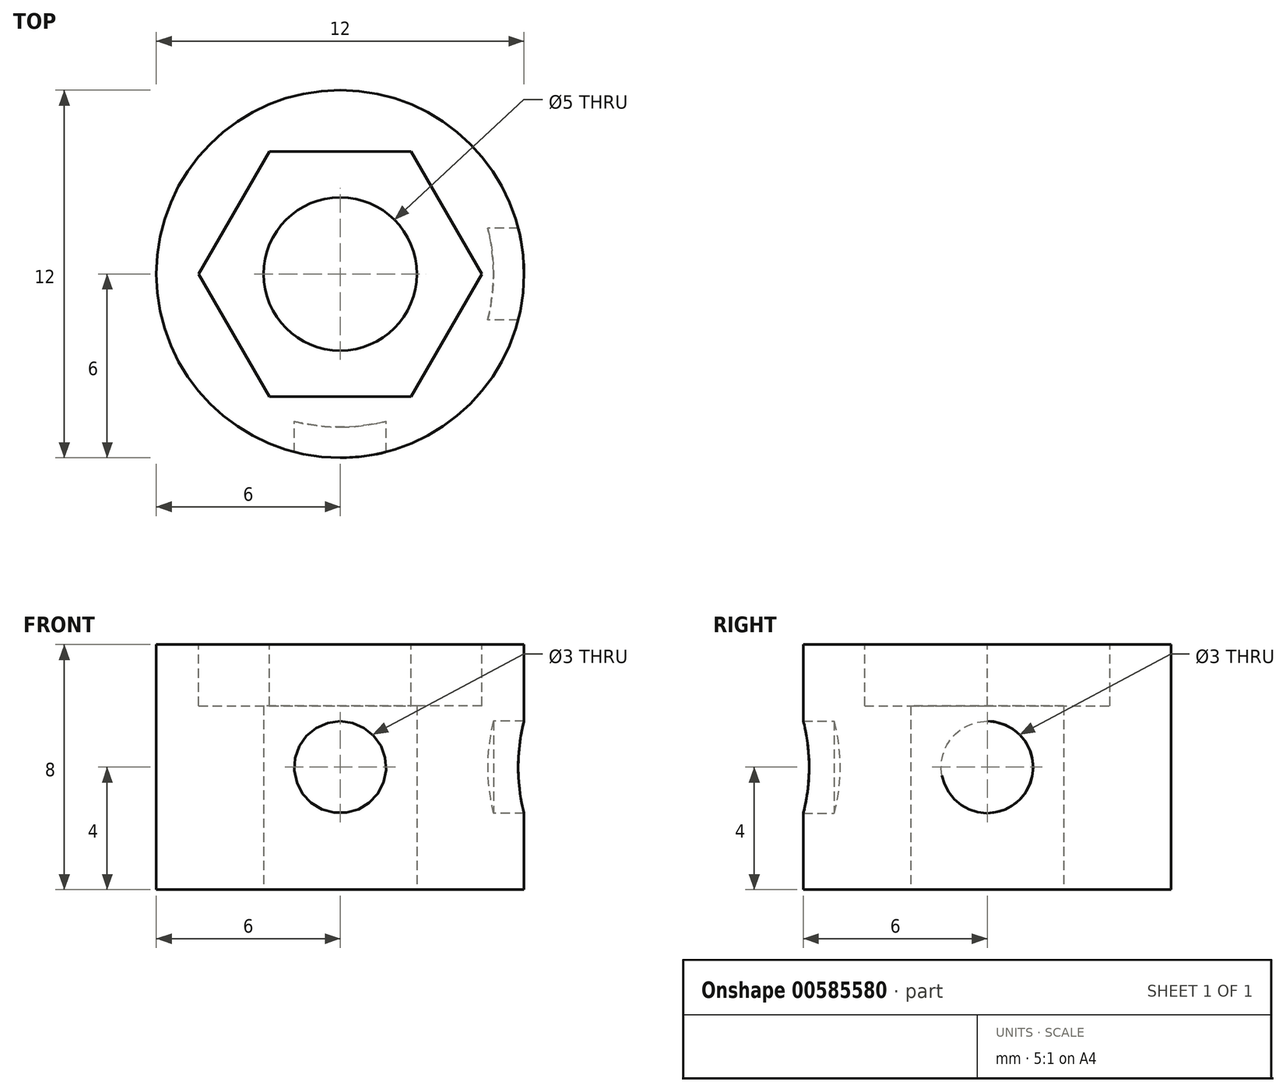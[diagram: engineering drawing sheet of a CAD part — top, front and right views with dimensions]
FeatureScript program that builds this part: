
annotation { "Feature Type Name" : "Feature", "Feature Type Description" : "" }
export const myFeature = defineFeature(function(context is Context, id is Id, definition is map)
    precondition{}
    {
        {
            var Q0;
            Q0=qCreatedBy(makeId("Top.planeOp"),FACE);
            var sketch = newSketch(context, id + "F0", { "sketchPlane" : qUnion([Q0])});
            skCircle(sketch, "E0", {"center": v(0, 0) * mm, "radius": 2.5 * mm});
            skCircle(sketch, "E1", {"center": v(0, 0) * mm, "radius": 6 * mm});
            skSolve(sketch);
        }
        {
            var Q0;
            Q0=makeQuery(id+"F0.imprint","IMPRINT",FACE,{"disambiguationData":[TD([[makeQuery(id+"F0.imprint","IMPRINT",EDGE,{"derivedFrom":sQuery(id+"F0.wireOp",EDGE,"E0")}),-1.0]])]});
            extrude(context, id + "F1", {"entities" : qUnion([Q0]), "depth" : 8 * mm, "offsetDistance" : 25 * mm});
        }
        {
            var Q0;
            Q0=qCreatedBy(makeId("Front.planeOp"),FACE);
            var sketch = newSketch(context, id + "F2", { "sketchPlane" : qUnion([Q0])});
            skLineSegment(sketch, "E2", {"start": v(-6, 0) * mm, "end": v(-6, 8) * mm, "construction": true});
            skCircle(sketch, "E3", {"center": v(0, 4) * mm, "radius": 1.5 * mm});
            skPoint(sketch, "E3.centerSnap0", {"position": v(-6, 4) * mm});
            skSolve(sketch);
        }
        {
            var Q0;
            Q0=makeQuery(id+"F2.imprint","IMPRINT",FACE,{"disambiguationData":[TD([[makeQuery(id+"F2.imprint","IMPRINT",EDGE,{"derivedFrom":sQuery(id+"F2.wireOp",EDGE,"E3")}),1.0]])]});
            var Q1;
            Q1=makeQuery(id+"F1.opExtrude","SWEPT_FACE",FACE,{"disambiguationData":[OSD([sQuery(id+"F0.wireOp",EDGE,"E1")])]});
            var Q2;
            Q2=makeQuery(id+"F1.opExtrude","SWEPT_FACE",FACE,{"disambiguationData":[OSD([sQuery(id+"F0.wireOp",EDGE,"E1")])]});
            extrude(context, id + "F3", {"entities" : qUnion([Q0]), "endBound" : BoundingType.UP_TO_SURFACE, "depth" : 25 * mm, "endBoundEntityFace" : qUnion([Q1]), "offsetDistance" : 25 * mm, "hasSecondDirection" : true, "secondDirectionBound" : SecondDirectionBoundingType.UP_TO_SURFACE, "secondDirectionOppositeDirection" : false, "secondDirectionDepth" : 25 * mm, "secondDirectionBoundEntityFace" : qUnion([Q2]), "hasSecondDirectionOffset" : true, "secondDirectionOffsetDistance" : 1 * mm});
        }
        {
            var Q0;
            Q0=makeQuery(id+"F3.opExtrude","SWEPT_BODY",BODY,{"disambiguationData":[OSD([sQuery(id+"F2.wireOp",EDGE,"E3")])]});
            var Q1;
            Q1=makeQuery(id+"F1.opExtrude","SWEPT_FACE",FACE,{"disambiguationData":[OSD([sQuery(id+"F0.wireOp",EDGE,"E0")])]});
            transform(context, id + "F4", {"entities" : qUnion([Q0]), "transformType" : TransformType.ROTATION, "transformAxis" : qUnion([Q1]), "angle" : 90 * degree, "makeCopy" : true});
        }
        {
            var Q0;
            Q0=makeQuery(id+"F3.opExtrude","SWEPT_BODY",BODY,{"disambiguationData":[OSD([sQuery(id+"F2.wireOp",EDGE,"E3")])]});
            var Q1;
            Q1=makeQuery(id+"F4.opPattern","COPY",BODY,{"derivedFrom":makeQuery(id+"F3.opExtrude","SWEPT_BODY",BODY,{"disambiguationData":[OSD([sQuery(id+"F2.wireOp",EDGE,"E3")])]}),"instanceName":"1"});
            var Q2;
            Q2=makeQuery(id+"F1.opExtrude","SWEPT_BODY",BODY,{"disambiguationData":[OSD([sQuery(id+"F0.wireOp",EDGE,"E0"),sQuery(id+"F0.wireOp",EDGE,"E1")])]});
            booleanBodies(context, id + "F5", {"operationType" : BooleanOperationType.SUBTRACTION, "tools" : qUnion([Q0, Q1]), "targets" : qUnion([Q2])});
        }
        {
            var Q0;
            Q0=makeQuery(id+"F1.opExtrude","CAP_FACE",FACE,{"disambiguationData":[OSD([sQuery(id+"F0.wireOp",EDGE,"E0"),sQuery(id+"F0.wireOp",EDGE,"E1")])],"isStart":false});
            var sketch = newSketch(context, id + "F6", { "sketchPlane" : qUnion([Q0])});
            skCircle(sketch, "E4.cCircle", {"center": v(0, 0) * mm, "radius": 4 * mm, "construction": true});
            skLineSegment(sketch, "E4.0", {"start": v(-2.3, 4) * mm, "end": v(2.3, 4) * mm});
            skLineSegment(sketch, "E4.1", {"start": v(2.3, 4) * mm, "end": v(4.62, 0) * mm});
            skLineSegment(sketch, "E4.2", {"start": v(4.62, 0) * mm, "end": v(2.3, -4) * mm});
            skLineSegment(sketch, "E4.3", {"start": v(2.3, -4) * mm, "end": v(-2.3, -4) * mm});
            skLineSegment(sketch, "E4.4", {"start": v(-2.3, -4) * mm, "end": v(-4.62, 0) * mm});
            skLineSegment(sketch, "E4.5", {"start": v(-4.62, 0) * mm, "end": v(-2.3, 4) * mm});
            skPoint(sketch, "E4.0.midPoint", {"position": v(0, 4) * mm});
            skSolve(sketch);
        }
        {
            var Q0;
            Q0=makeQuery(id+"F6.imprint","IMPRINT",FACE,{"disambiguationData":[TD([[makeQuery(id+"F6.imprint","IMPRINT",EDGE,{"derivedFrom":sQuery(id+"F6.wireOp",EDGE,"E4.0")}),-1.0]])]});
            extrude(context, id + "F7", {"entities" : qUnion([Q0]), "operationType" : NewBodyOperationType.REMOVE, "oppositeDirection" : true, "depth" : 2 * mm, "offsetDistance" : 25 * mm});
        }
    });
